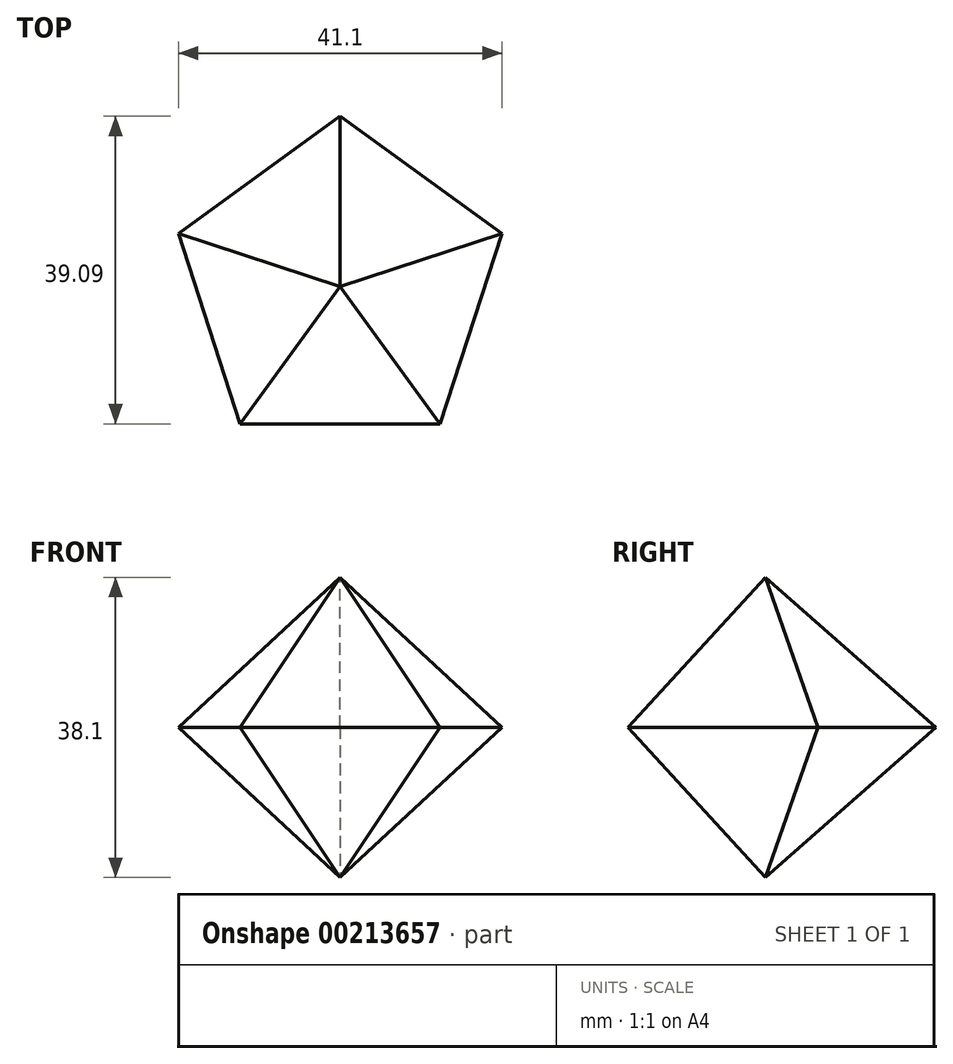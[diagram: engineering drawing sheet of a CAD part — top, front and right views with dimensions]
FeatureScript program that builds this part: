
annotation { "Feature Type Name" : "Feature", "Feature Type Description" : "" }
export const myFeature = defineFeature(function(context is Context, id is Id, definition is map)
    precondition{}
    {
        {
            var Q0;
            Q0=qCreatedBy(makeId("Top.planeOp"),FACE);
            var sketch = newSketch(context, id + "F0", { "sketchPlane" : qUnion([Q0])});
            skCircle(sketch, "E0.cCircle", {"center": v(0, 0) * mm, "radius": 17.48 * mm, "construction": true});
            skLineSegment(sketch, "E0.0", {"start": v(20.55, 6.68) * mm, "end": v(12.7, -17.48) * mm});
            skLineSegment(sketch, "E0.1", {"start": v(12.7, -17.48) * mm, "end": v(-12.7, -17.48) * mm});
            skLineSegment(sketch, "E0.2", {"start": v(-12.7, -17.48) * mm, "end": v(-20.55, 6.68) * mm});
            skLineSegment(sketch, "E0.3", {"start": v(-20.55, 6.68) * mm, "end": v(0, 21.6) * mm});
            skLineSegment(sketch, "E0.4", {"start": v(0, 21.6) * mm, "end": v(20.55, 6.68) * mm});
            skPoint(sketch, "E0.0.midPoint", {"position": v(16.62, -5.4) * mm});
            skSolve(sketch);
        }
        {
            var Q0;
            Q0=qCreatedBy(makeId("Front.planeOp"),FACE);
            var sketch = newSketch(context, id + "F1", { "sketchPlane" : qUnion([Q0])});
            skPoint(sketch, "E1", {"position": v(0, -19.05) * mm});
            skPoint(sketch, "E2", {"position": v(0, 19.05) * mm});
            skSolve(sketch);
        }
        {
            var Q0;
            Q0=makeQuery(id+"F0.imprint","IMPRINT",FACE,{"disambiguationData":[TD([[makeQuery(id+"F0.imprint","IMPRINT",EDGE,{"derivedFrom":sQuery(id+"F0.wireOp",EDGE,"E0.0")}),-1.0]])]});
            var Q1;
            Q1=sQuery(id+"F1.wireOp",VERTEX,"E2");
            var Q2;
            Q2=sQuery(id+"F0.wireOp",VERTEX,"E0.1.start");
            var Q3;
            Q3=sQuery(id+"F0.wireOp",VERTEX,"E0.2.start");
            var Q4;
            Q4=sQuery(id+"F0.wireOp",VERTEX,"E0.3.start");
            var Q5;
            Q5=sQuery(id+"F0.wireOp",VERTEX,"E0.4.start");
            var Q6;
            Q6=sQuery(id+"F0.wireOp",VERTEX,"E0.4.end");
            loft(context, id + "F2", {"sheetProfilesArray" : [{ "sheetProfileEntities" : qUnion([Q0]) }, { "sheetProfileEntities" : qUnion([Q1]) }], "connections" : [{ "connectionEntities" : qUnion([Q2, Q3, Q4, Q5, Q6]), "connectionEdgeQueries" : qUnion([]), "connectionEdgeParameters" : [] }]});
        }
        {
            var Q1;
            Q1 = qSketchRegion(id + "F0", true);
            var Q2;
            Q2=sQuery(id+"F1.wireOp",VERTEX,"E1");
            loft(context, id + "F3", {"operationType" : NewBodyOperationType.ADD, "sheetProfilesArray" : [{ "sheetProfileEntities" : qUnion([Q1]) }, { "sheetProfileEntities" : qUnion([Q2]) }]});
        }
    });
